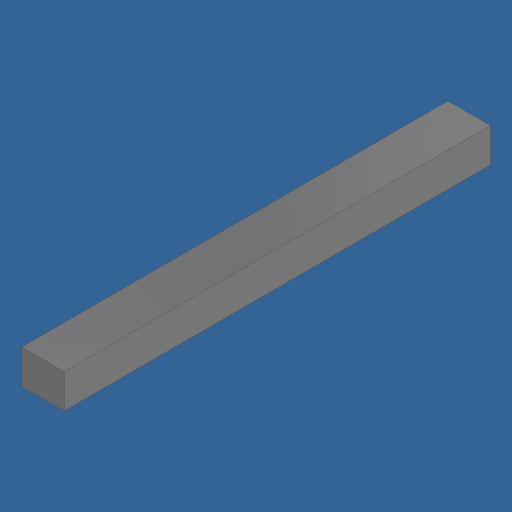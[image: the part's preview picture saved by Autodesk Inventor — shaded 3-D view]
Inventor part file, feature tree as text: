
AUTODESK INVENTOR PART (.ipt)
format: ipt  version: 2024 (Build 280153000, 153)  size: 223,232 bytes
history: native  units: in
note: dims shown in document units (in); Inventor stores cm internally (conversion verified against a paired STEP export)
features: extrude x1
ambient origin geometry x8: Origin, YZ Plane, XZ Plane, XY Plane, X Axis, Y Axis, Z Axis, Center Point
bodies: Solid1 (feature_tree)
feature tree (1):
  extrude  "Extrusion1"  Depth=0.0394in
